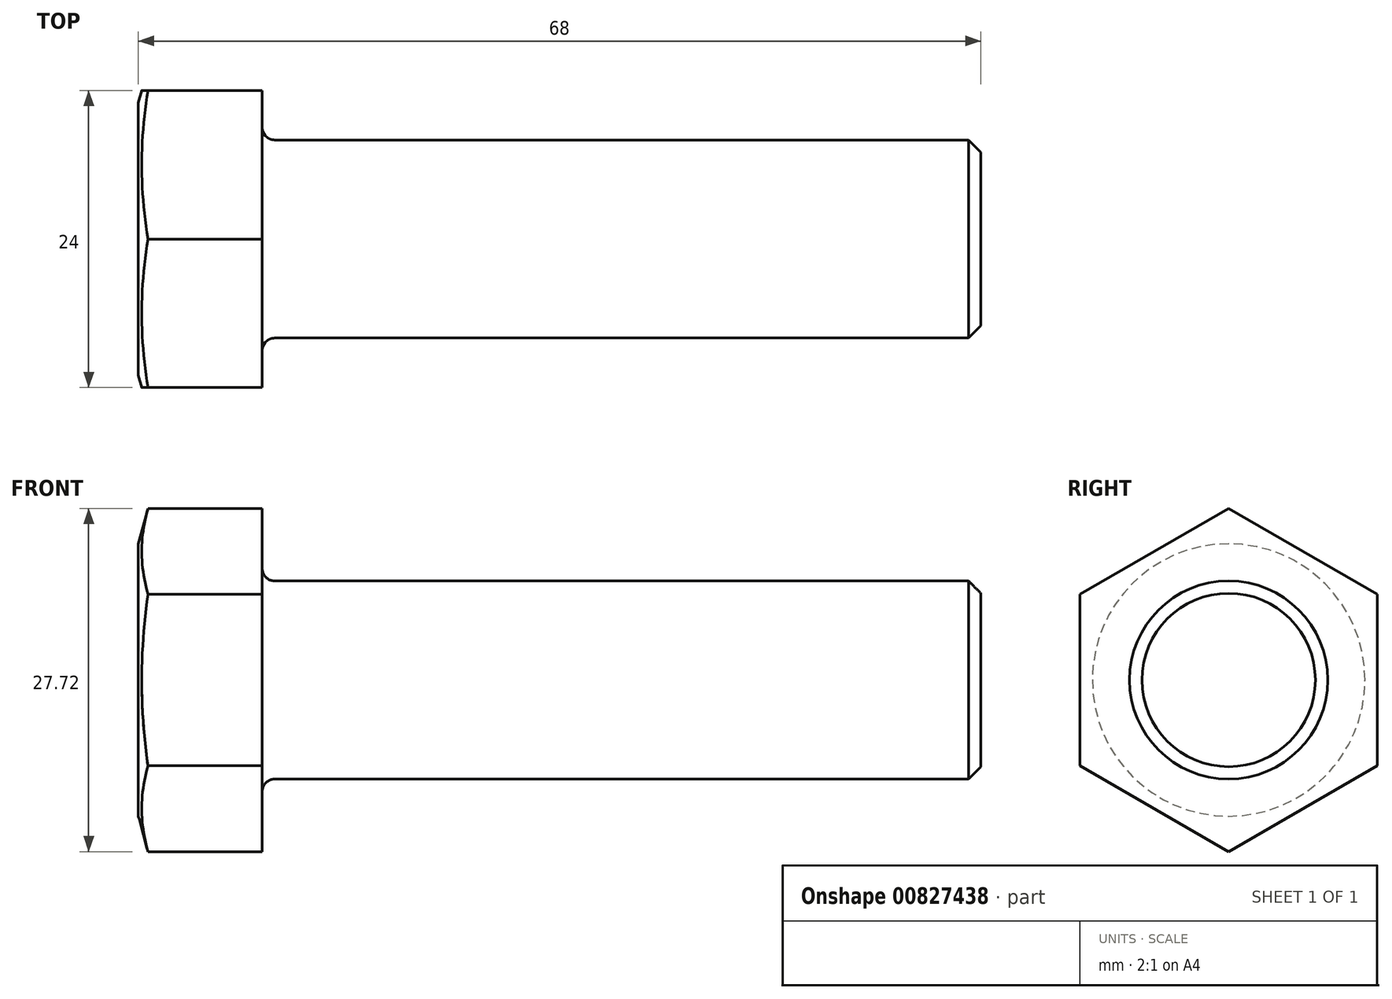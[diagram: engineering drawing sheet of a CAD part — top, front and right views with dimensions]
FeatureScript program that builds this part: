
annotation { "Feature Type Name" : "Feature", "Feature Type Description" : "" }
export const myFeature = defineFeature(function(context is Context, id is Id, definition is map)
    precondition{}
    {
        {
            var Q0;
            Q0=qCreatedBy(makeId("Front.planeOp"),FACE);
            var sketch = newSketch(context, id + "F0", { "sketchPlane" : qUnion([Q0])});
            skLineSegment(sketch, "E0", {"start": v(0, 0) * mm, "end": v(68, 0) * mm});
            skLineSegment(sketch, "E1", {"start": v(68, 0) * mm, "end": v(68, 8) * mm});
            skLineSegment(sketch, "E2", {"start": v(68, 8) * mm, "end": v(10, 8) * mm});
            skLineSegment(sketch, "E3", {"start": v(10, 8) * mm, "end": v(10, 14) * mm});
            skLineSegment(sketch, "E4", {"start": v(10, 14) * mm, "end": v(0, 14) * mm});
            skLineSegment(sketch, "E5", {"start": v(0, 14) * mm, "end": v(0, 0) * mm});
            skSolve(sketch);
        }
        {
            var Q0;
            Q0=makeQuery(id+"F0.imprint","IMPRINT",FACE,{"disambiguationData":[TD([[makeQuery(id+"F0.imprint","IMPRINT",EDGE,{"derivedFrom":sQuery(id+"F0.wireOp",EDGE,"E0")}),1.0]])]});
            var Q1;
            Q1=sQuery(id+"F0.wireOp",EDGE,"E0");
            revolve(context, id + "F1", {"surfaceOperationType" : NewSurfaceOperationType.NEW, "entities" : qUnion([Q0]), "axis" : qUnion([Q1]), "revolveType" : RevolveType.FULL});
        }
        {
            var Q0;
            Q0=makeQuery(id+"F1.opRevolve","SWEPT_FACE",FACE,{"disambiguationData":[OSD([sQuery(id+"F0.wireOp",EDGE,"E5")])]});
            var sketch = newSketch(context, id + "F2", { "sketchPlane" : qUnion([Q0])});
            skCircle(sketch, "E6.cCircle", {"center": v(0, 0) * mm, "radius": 13.86 * mm, "construction": true});
            skLineSegment(sketch, "E6.0", {"start": v(0, 13.86) * mm, "end": v(12, 6.93) * mm});
            skLineSegment(sketch, "E6.1", {"start": v(12, 6.93) * mm, "end": v(12, -6.93) * mm});
            skLineSegment(sketch, "E6.2", {"start": v(12, -6.93) * mm, "end": v(0, -13.86) * mm});
            skLineSegment(sketch, "E6.3", {"start": v(0, -13.86) * mm, "end": v(-12, -6.93) * mm});
            skLineSegment(sketch, "E6.4", {"start": v(-12, -6.93) * mm, "end": v(-12, 6.93) * mm});
            skLineSegment(sketch, "E6.5", {"start": v(-12, 6.93) * mm, "end": v(0, 13.86) * mm});
            skSolve(sketch);
        }
        {
            var Q0;
            Q0=makeQuery(id+"F2.imprint","IMPRINT",FACE,{"disambiguationData":[TD([[makeQuery(id+"F2.imprint","IMPRINT",EDGE,{"derivedFrom":sQuery(id+"F2.wireOp",EDGE,"E6.0")}),1.0]])]});
            extrude(context, id + "F3", {"entities" : qUnion([Q0]), "operationType" : NewBodyOperationType.REMOVE, "oppositeDirection" : true, "depth" : 25 * mm, "offsetDistance" : 25 * mm});
        }
        {
            var Q0;
            Q0=makeQuery(id+"F1.opRevolve","SWEPT_EDGE",EDGE,{"disambiguationData":[OSD([sQuery(id+"F0.wireOp",EDGE,"E1"),sQuery(id+"F0.wireOp",EDGE,"E2")])]});
            chamfer(context, id + "F4", {"entities" : qUnion([Q0]), "width" : 1 * mm, "tangentPropagation" : true});
        }
        {
            var Q0;
            Q0=makeQuery(id+"F1.opRevolve","SWEPT_EDGE",EDGE,{"disambiguationData":[OSD([sQuery(id+"F0.wireOp",EDGE,"E2"),sQuery(id+"F0.wireOp",EDGE,"E3")])]});
            fillet(context, id + "F5", {"entities" : qUnion([Q0]), "radius" : 1 * mm, "tangentPropagation" : true, "allowEdgeOverflow" : false});
        }
        {
            var Q0;
            Q0=qCreatedBy(makeId("Front.planeOp"),FACE);
            var sketch = newSketch(context, id + "F6", { "sketchPlane" : qUnion([Q0])});
            skLineSegment(sketch, "E7", {"start": v(0, 11) * mm, "end": v(4.21, 26.71) * mm});
            skLineSegment(sketch, "E8", {"start": v(4.21, 26.71) * mm, "end": v(0, 26.71) * mm});
            skLineSegment(sketch, "E9", {"start": v(0, 26.71) * mm, "end": v(0, 11) * mm});
            skLineSegment(sketch, "E10", {"start": v(0, 0) * mm, "end": v(88.31, 0) * mm, "construction": true});
            skSolve(sketch);
        }
        {
            var Q0;
            Q0=makeQuery(id+"F6.imprint","IMPRINT",FACE,{"disambiguationData":[TD([[makeQuery(id+"F6.imprint","IMPRINT",EDGE,{"derivedFrom":sQuery(id+"F6.wireOp",EDGE,"E7")}),1.0]])]});
            var Q1;
            Q1=sQuery(id+"F6.wireOp",EDGE,"E10");
            revolve(context, id + "F7", {"operationType" : NewBodyOperationType.REMOVE, "surfaceOperationType" : NewSurfaceOperationType.NEW, "entities" : qUnion([Q0]), "axis" : qUnion([Q1]), "revolveType" : RevolveType.FULL, "oppositeDirection" : true});
        }
    });
